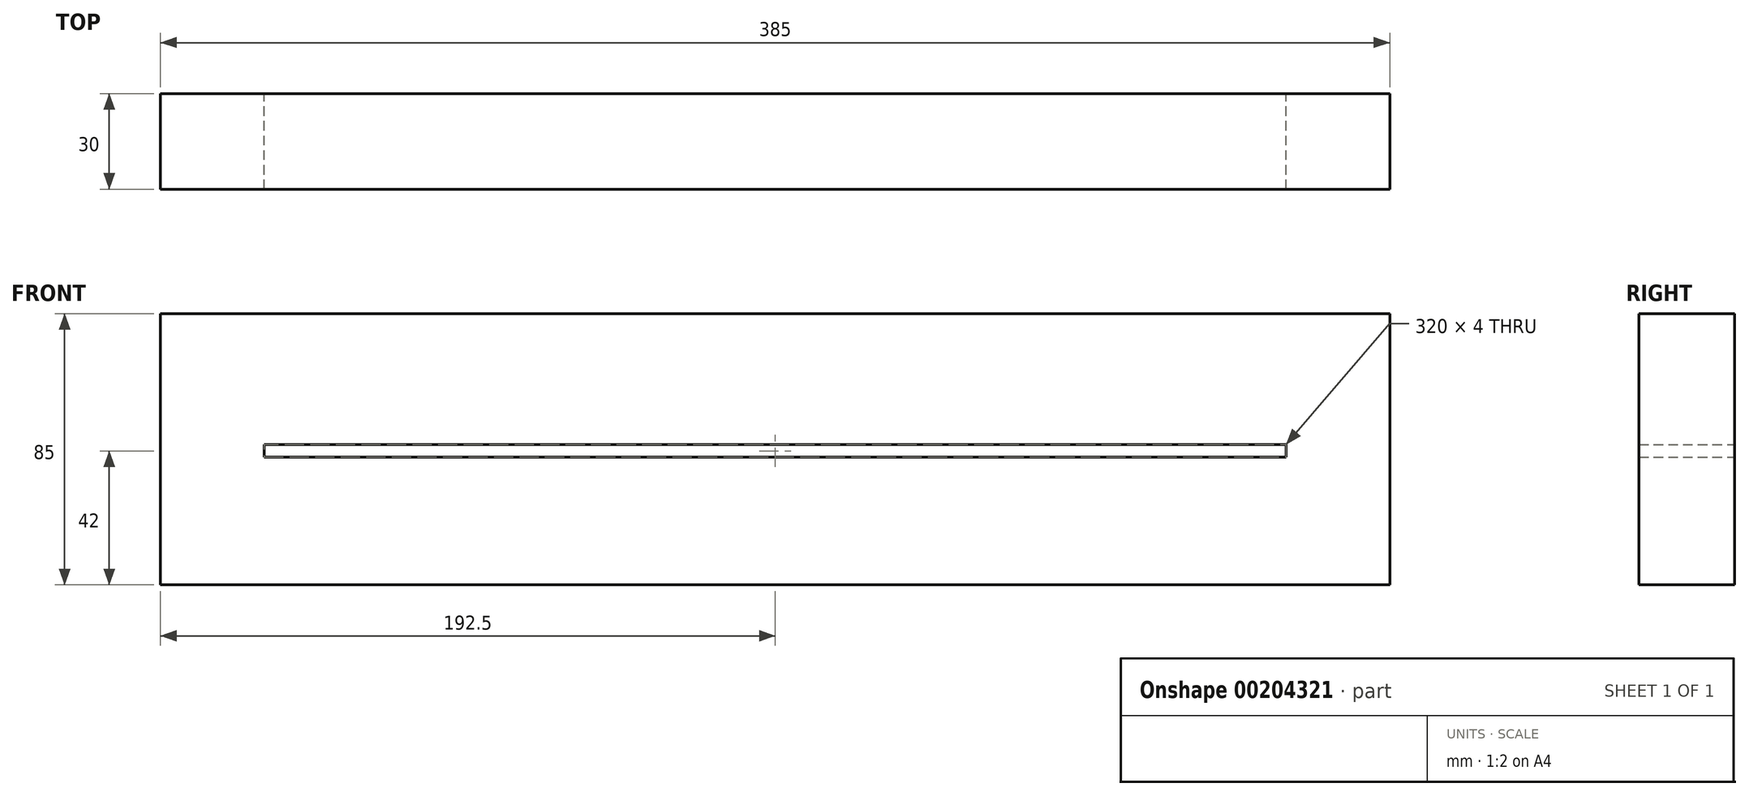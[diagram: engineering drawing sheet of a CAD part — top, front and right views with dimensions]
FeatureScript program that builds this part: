
annotation { "Feature Type Name" : "Feature", "Feature Type Description" : "" }
export const myFeature = defineFeature(function(context is Context, id is Id, definition is map)
    precondition{}
    {
        {
            var Q0;
            Q0=qCreatedBy(makeId("Front.planeOp"),FACE);
            var sketch = newSketch(context, id + "F0", { "sketchPlane" : qUnion([Q0])});
            skLineSegment(sketch, "E0.bottom", {"start": v(0, 0) * mm, "end": v(385, 0) * mm});
            skLineSegment(sketch, "E0.top", {"start": v(0, 85) * mm, "end": v(385, 85) * mm});
            skLineSegment(sketch, "E0.left", {"start": v(0, 0) * mm, "end": v(0, 85) * mm});
            skLineSegment(sketch, "E0.right", {"start": v(385, 0) * mm, "end": v(385, 85) * mm});
            skLineSegment(sketch, "E1.bottom", {"start": v(32.5, 44) * mm, "end": v(352.5, 44) * mm});
            skLineSegment(sketch, "E1.top", {"start": v(32.5, 40) * mm, "end": v(352.5, 40) * mm});
            skLineSegment(sketch, "E1.left", {"start": v(32.5, 44) * mm, "end": v(32.5, 40) * mm});
            skLineSegment(sketch, "E1.right", {"start": v(352.5, 44) * mm, "end": v(352.5, 40) * mm});
            skSolve(sketch);
        }
        {
            var Q0;
            Q0=makeQuery(id+"F0.imprint","IMPRINT",FACE,{"disambiguationData":[TD([[makeQuery(id+"F0.imprint","IMPRINT",EDGE,{"derivedFrom":sQuery(id+"F0.wireOp",EDGE,"E0.bottom")}),1.0]])]});
            extrude(context, id + "F1", {"entities" : qUnion([Q0]), "depth" : 30 * mm});
        }
    });
